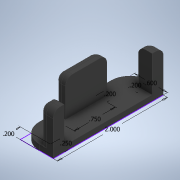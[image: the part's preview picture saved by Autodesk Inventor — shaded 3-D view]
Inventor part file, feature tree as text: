
AUTODESK INVENTOR PART (.ipt)
format: ipt  version: 2020 (Build 240168000, 168)  size: 171,008 bytes
history: native  units: in
note: dims shown in document units (in); Inventor stores cm internally (conversion verified against a paired STEP export)
features: extrude x2, fillet x2, sketch x1
ambient origin geometry x8: Origin, YZ Plane, XZ Plane, XY Plane, X Axis, Y Axis, Z Axis, Center Point
bodies: Solid1 (feature_tree)
feature tree (5):
  sketch  "Sketch1"  dims[d0=0.6in d1=2.0in d2=0.25in d3=0.2in d4=0.2in d8=0.2in d9=0.75in d10=0.75in d11=0.0in d12=0.1in d13=0.0in d14=0.35in d15=0.125in]
  extrude  "Extrusion1"  Depth=2.0in
  extrude  "Extrusion2"  Depth=0.25in
  fillet  "Fillet1"  Radius=0.2in
  fillet  "Fillet2"  Radius=0.2in
